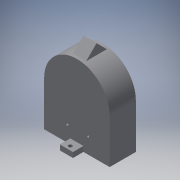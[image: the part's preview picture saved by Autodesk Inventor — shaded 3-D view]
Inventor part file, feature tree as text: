
AUTODESK INVENTOR PART (.ipt)
format: ipt  version: 2016 (Build 200138000, 138)  size: 162,304 bytes
history: native  units: in
note: dims shown in document units (in); Inventor stores cm internally (conversion verified against a paired STEP export)
features: extrude x7, sketch x6, reference x4, plane x1
ambient origin geometry x8: Origin, YZ Plane, XZ Plane, XY Plane, X Axis, Y Axis, Z Axis, Center Point
bodies: Solid1 (feature_tree)
feature tree (18):
  extrude  "Extrusion1"  Depth=1.0in TaperAngle=0.0deg
  extrude  "Extrusion4"  Depth=0.4in TaperAngle=0.0deg
  extrude  "Extrusion5"  Depth=0.1772in
  extrude  "Extrusion6"  Depth=0.4in
  extrude  "Extrusion8"  Depth=0.197in
  plane  "Work Plane1"
  extrude  "Extrusion9"  Depth=0.5in
  extrude  "Extrusion10"  Depth=1.0in
  sketch  "Sketch1"  dims[d0=2.5in d1=1.0in d2=0.0in]
  reference  "Reference1"
  sketch  "Sketch2"  dims[d9=0.197in d10=0.4in d11=0.0in]
  reference  "Reference2"
  sketch  "Sketch4"  dims[d12=0.15in d13=0.1772in]
  sketch  "Sketch7"  dims[d14=0.4in d15=0.0in d16=0.25in]
  sketch  "Sketch8"  dims[d17=0.5in d18=0.197in]
  sketch  "Sketch9"  dims[d19=0.4in d20=0.0in d25=0.5in d26=0.25in d27=0.5in d28=0.197in d29=0.15in d30=0.1378in d31=0.4in d32=0.0in d33=-1.25in d34=0.1065in d35=0.787in d36=0.394in d37=0.394in d38=0.5in d39=0.0in d40=0.0787in d41=0.0787in d42=1.0in d43=0.0in d44=0.098in]
  reference  "Reference3"
  reference  "Reference4"
